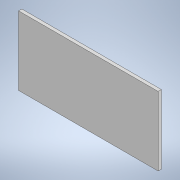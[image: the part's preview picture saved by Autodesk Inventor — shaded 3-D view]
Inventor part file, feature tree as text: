
AUTODESK INVENTOR PART (.ipt)
format: ipt  version: 2021 (Build 250183000, 183)  size: 88,576 bytes
history: native  units: mm
features: extrude x1, sketch x1
ambient origin geometry x8: Origin, YZ Plane, XZ Plane, XY Plane, X Axis, Y Axis, Z Axis, Center Point
bodies: Solid1 (feature_tree)
feature tree (2):
  extrude  "Extrusion1"  Depth=42.5mm
  sketch  "Sketch1"  dims[d0=86.0mm d1=42.5mm d2=2.0mm d3=0.0mm]
